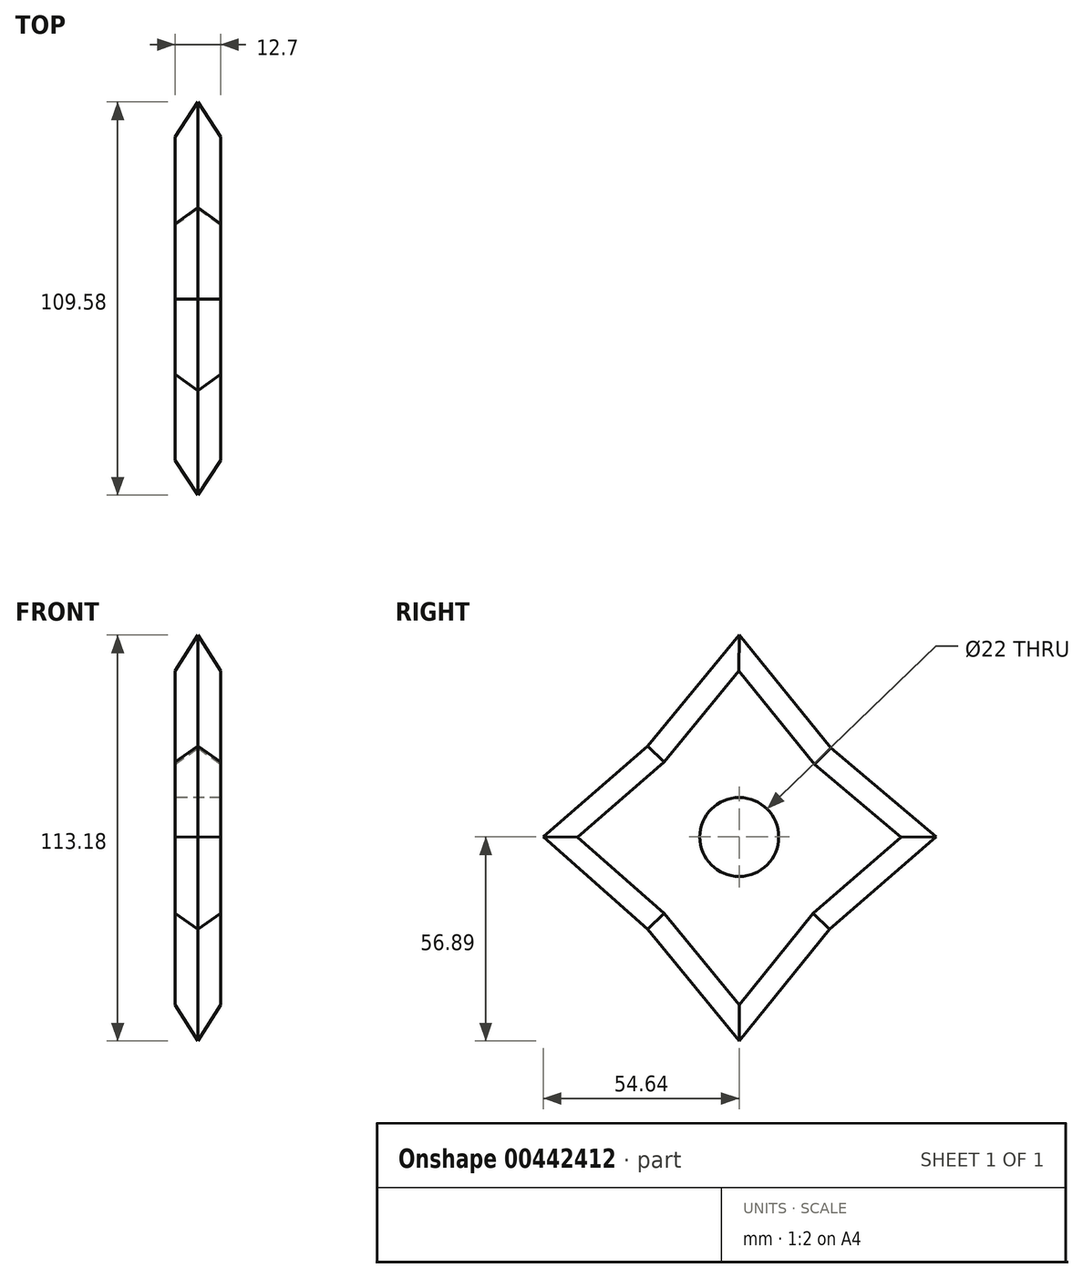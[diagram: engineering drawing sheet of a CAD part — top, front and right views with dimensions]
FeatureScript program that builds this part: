
annotation { "Feature Type Name" : "Feature", "Feature Type Description" : "" }
export const myFeature = defineFeature(function(context is Context, id is Id, definition is map)
    precondition{}
    {
        {
            var Q0;
            Q0=qCreatedBy(makeId("Right.planeOp"),FACE);
            var sketch = newSketch(context, id + "F0", { "sketchPlane" : qUnion([Q0])});
            skLineSegment(sketch, "E0", {"start": v(-25.52, 25.37) * mm, "end": v(0, 56.3) * mm});
            skLineSegment(sketch, "E1", {"start": v(0, 56.3) * mm, "end": v(25.52, 24.77) * mm});
            skLineSegment(sketch, "E2", {"start": v(-25.52, 25.37) * mm, "end": v(-54.64, 0) * mm});
            skLineSegment(sketch, "E3", {"start": v(-54.64, 0) * mm, "end": v(-25.52, -25.67) * mm});
            skLineSegment(sketch, "E4", {"start": v(-25.52, -25.67) * mm, "end": v(0, -56.9) * mm});
            skLineSegment(sketch, "E5", {"start": v(0, -56.9) * mm, "end": v(25.22, -25.67) * mm});
            skLineSegment(sketch, "E6", {"start": v(25.22, -25.67) * mm, "end": v(54.94, 0) * mm});
            skLineSegment(sketch, "E7", {"start": v(54.94, 0) * mm, "end": v(25.52, 24.77) * mm});
            skSolve(sketch);
        }
        {
            var Q0;
            Q0=makeQuery(id+"F0.imprint","IMPRINT",FACE,{"disambiguationData":[TD([[makeQuery(id+"F0.imprint","IMPRINT",EDGE,{"derivedFrom":sQuery(id+"F0.wireOp",EDGE,"E0")}),-1.0]])]});
            extrude(context, id + "F1", {"entities" : qUnion([Q0]), "depth" : 12.7 * mm});
        }
        {
            var Q0;
            Q0=makeQuery(id+"F1.opExtrude","CAP_EDGE",EDGE,{"disambiguationData":[OSD([sQuery(id+"F0.wireOp",EDGE,"E2")])],"isStart":false});
            var Q1;
            Q1=makeQuery(id+"F1.opExtrude","CAP_EDGE",EDGE,{"disambiguationData":[OSD([sQuery(id+"F0.wireOp",EDGE,"E2")])],"isStart":true});
            var Q2;
            Q2=makeQuery(id+"F1.opExtrude","CAP_EDGE",EDGE,{"disambiguationData":[OSD([sQuery(id+"F0.wireOp",EDGE,"E3")])],"isStart":false});
            var Q3;
            Q3=makeQuery(id+"F1.opExtrude","CAP_EDGE",EDGE,{"disambiguationData":[OSD([sQuery(id+"F0.wireOp",EDGE,"E3")])],"isStart":true});
            var Q4;
            Q4=makeQuery(id+"F1.opExtrude","CAP_EDGE",EDGE,{"disambiguationData":[OSD([sQuery(id+"F0.wireOp",EDGE,"E4")])],"isStart":false});
            var Q5;
            Q5=makeQuery(id+"F1.opExtrude","CAP_EDGE",EDGE,{"disambiguationData":[OSD([sQuery(id+"F0.wireOp",EDGE,"E4")])],"isStart":true});
            var Q6;
            Q6=makeQuery(id+"F1.opExtrude","CAP_EDGE",EDGE,{"disambiguationData":[OSD([sQuery(id+"F0.wireOp",EDGE,"E5")])],"isStart":true});
            var Q7;
            Q7=makeQuery(id+"F1.opExtrude","CAP_EDGE",EDGE,{"disambiguationData":[OSD([sQuery(id+"F0.wireOp",EDGE,"E5")])],"isStart":false});
            var Q8;
            Q8=makeQuery(id+"F1.opExtrude","CAP_EDGE",EDGE,{"disambiguationData":[OSD([sQuery(id+"F0.wireOp",EDGE,"E6")])],"isStart":true});
            var Q9;
            Q9=makeQuery(id+"F1.opExtrude","CAP_EDGE",EDGE,{"disambiguationData":[OSD([sQuery(id+"F0.wireOp",EDGE,"E6")])],"isStart":false});
            var Q10;
            Q10=makeQuery(id+"F1.opExtrude","CAP_EDGE",EDGE,{"disambiguationData":[OSD([sQuery(id+"F0.wireOp",EDGE,"E7")])],"isStart":false});
            var Q11;
            Q11=makeQuery(id+"F1.opExtrude","CAP_EDGE",EDGE,{"disambiguationData":[OSD([sQuery(id+"F0.wireOp",EDGE,"E7")])],"isStart":true});
            var Q12;
            Q12=makeQuery(id+"F1.opExtrude","CAP_EDGE",EDGE,{"disambiguationData":[OSD([sQuery(id+"F0.wireOp",EDGE,"E1")])],"isStart":true});
            var Q13;
            Q13=makeQuery(id+"F1.opExtrude","CAP_EDGE",EDGE,{"disambiguationData":[OSD([sQuery(id+"F0.wireOp",EDGE,"E1")])],"isStart":false});
            var Q14;
            Q14=makeQuery(id+"F1.opExtrude","CAP_EDGE",EDGE,{"disambiguationData":[OSD([sQuery(id+"F0.wireOp",EDGE,"E0")])],"isStart":true});
            var Q15;
            Q15=makeQuery(id+"F1.opExtrude","CAP_EDGE",EDGE,{"disambiguationData":[OSD([sQuery(id+"F0.wireOp",EDGE,"E0")])],"isStart":false});
            chamfer(context, id + "F2", {"entities" : qUnion([Q0, Q1, Q2, Q3, Q4, Q5, Q6, Q7, Q8, Q9, Q10, Q11, Q12, Q13, Q14, Q15]), "width" : 6.35 * mm, "tangentPropagation" : true});
        }
        {
            var Q0;
            Q0=qCreatedBy(makeId("Right.planeOp"),FACE);
            var sketch = newSketch(context, id + "F3", { "sketchPlane" : qUnion([Q0])});
            skPoint(sketch, "E8", {"position": v(0, 0) * mm});
            skSolve(sketch);
        }
        {
            var Q0;
            Q0=sQuery(id+"F3.wireOp",VERTEX,"E8");
            var Q1;
            Q1=makeQuery(id+"F1.opExtrude","SWEPT_BODY",BODY,{"disambiguationData":[OSD([sQuery(id+"F0.wireOp",EDGE,"E0"),sQuery(id+"F0.wireOp",EDGE,"E1"),sQuery(id+"F0.wireOp",EDGE,"E2"),sQuery(id+"F0.wireOp",EDGE,"E3"),sQuery(id+"F0.wireOp",EDGE,"E4"),sQuery(id+"F0.wireOp",EDGE,"E5"),sQuery(id+"F0.wireOp",EDGE,"E6"),sQuery(id+"F0.wireOp",EDGE,"E7")])]});
            hole(context, id + "F4", {"style" : HoleStyle.SIMPLE, "endStyle" : HoleEndStyle.THROUGH, "oppositeDirection" : true, "standardTappedOrClearance" : lookupTablePath({ "standard" : "ISO", "fit" : "Normal", "size" : "M20", "type" : "Clearance" }), "standardBlindInLast" : lookupTablePath({ "fit" : "Standard", "standard" : "ISO", "size" : "M20", "type" : "Clearance" }), "holeDiameter" : 22 * mm, "isTappedThrough" : true, "tappedDepth" : 12.7 * mm, "tapClearance" : 3, "locations" : qUnion([Q0]), "scope" : qUnion([Q1])});
        }
    });
